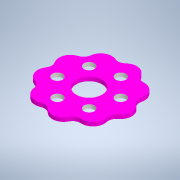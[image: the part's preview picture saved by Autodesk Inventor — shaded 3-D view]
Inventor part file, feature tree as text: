
AUTODESK INVENTOR PART (.ipt)
format: ipt  version: 2022 (Build 260153000, 153)  size: 179,200 bytes
history: native  units: in
note: dims shown in document units (in); Inventor stores cm internally (conversion verified against a paired STEP export)
features: extrude x3, sketch x3, other x1
ambient origin geometry x8: Origin, YZ Plane, XZ Plane, XY Plane, X Axis, Y Axis, Z Axis, Center Point
bodies: Solid1 (feature_tree)
feature tree (7):
  extrude  "Extrusion1"  Depth=0.1181in TaperAngle=0.0deg
  extrude  "Extrusion2"  Depth=0.1181in TaperAngle=0.0deg
  extrude  "Extrusion3"  TaperAngle=45.0deg  [1 undecoded]
  sketch  "Sketch1"  dims[d0=0.0in d1=141.7323in d2=0.1181in d3=0.0in]
  other  "2D Equation Curve1"
  sketch  "Sketch2"  dims[d4=0.7874in d5=0.1181in d6=0.0in]
  sketch  "Sketch3"  dims[d7=1.5748in d8=45.0deg d9=0.315in d10=2.3622in d12=360.0deg d14=0.3937in d15=0.0in]
note: 1 required parameter value undecoded (feature->parameter linkage not recoverable at this tier; creation-order binding heuristic only, values carry confidence <= 0.55)
